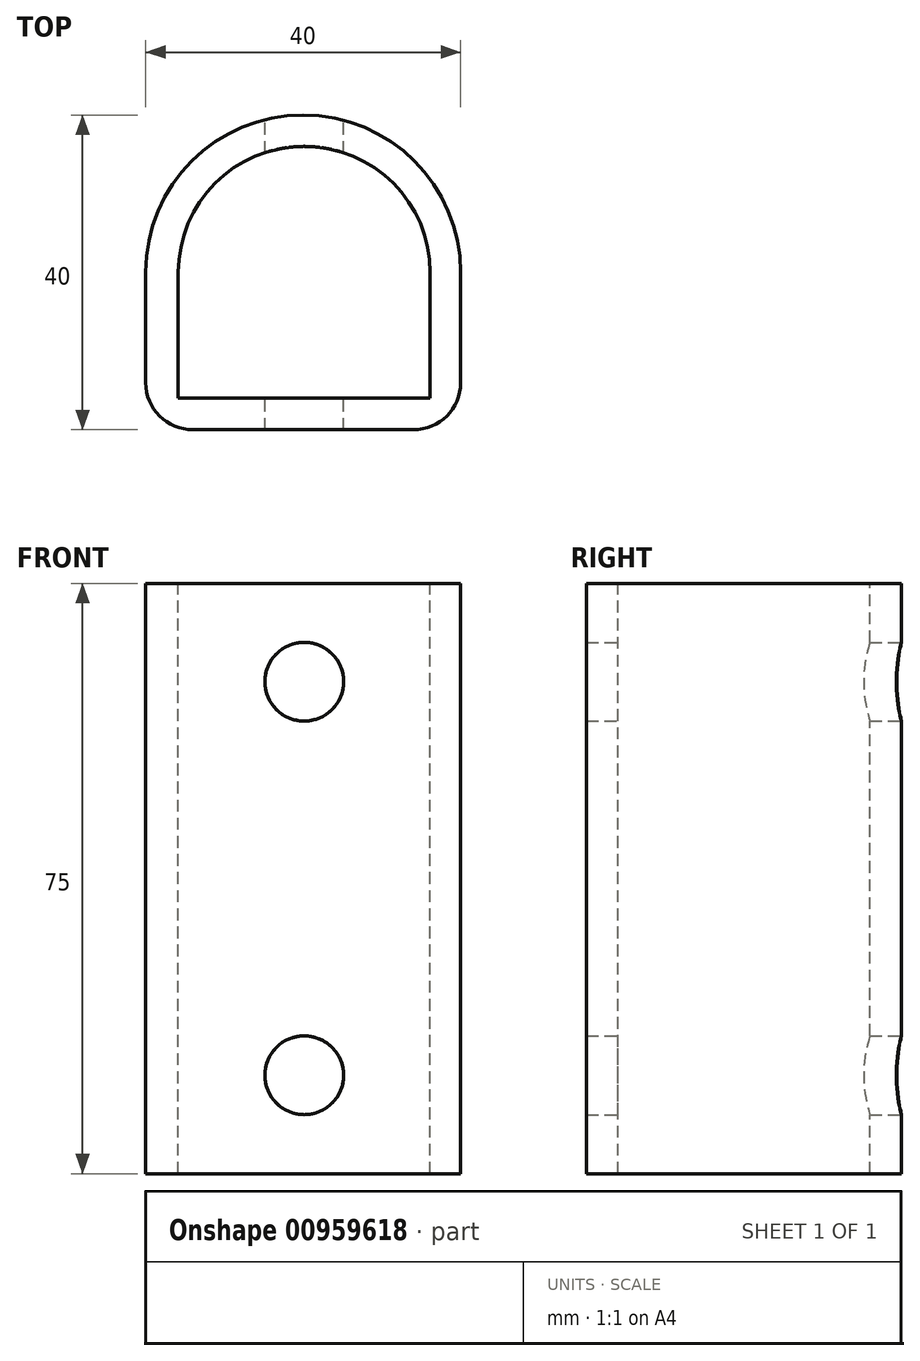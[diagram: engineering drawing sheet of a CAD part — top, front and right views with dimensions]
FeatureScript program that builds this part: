
annotation { "Feature Type Name" : "Feature", "Feature Type Description" : "" }
export const myFeature = defineFeature(function(context is Context, id is Id, definition is map)
    precondition{}
    {
        {
            var Q0;
            Q0=qCreatedBy(makeId("Top.planeOp"),FACE);
            var sketch = newSketch(context, id + "F0", { "sketchPlane" : qUnion([Q0])});
            skLineSegment(sketch, "E0", {"start": v(0, 0) * mm, "end": v(40, 0) * mm});
            skLineSegment(sketch, "E1", {"start": v(40, 0) * mm, "end": v(40, 20) * mm});
            skLineSegment(sketch, "E2", {"start": v(40, 20) * mm, "end": v(0, 20) * mm});
            skLineSegment(sketch, "E3", {"start": v(0, 20) * mm, "end": v(0, 0) * mm});
            skCircle(sketch, "E4", {"center": v(20, 20) * mm, "radius": 20 * mm});
            skSolve(sketch);
        }
        {
            var Q0;
            {var subQ0=sQuery(id+"F0.wireOp",EDGE,"E2");Q0=makeQuery(id+"F0.imprint","IMPRINT",FACE,{"disambiguationData":[TD([[makeQuery(id+"F0.imprint","IMPRINT",EDGE,{"derivedFrom":subQ0}),-1.0]])]});}
            var Q1;
            {var subQ0=sQuery(id+"F0.wireOp",EDGE,"E2");Q1=makeQuery(id+"F0.imprint","IMPRINT",FACE,{"disambiguationData":[TD([[makeQuery(id+"F0.imprint","IMPRINT",EDGE,{"derivedFrom":subQ0}),1.0]])]});}
            var Q2;
            {var subQ0=sQuery(id+"F0.wireOp",EDGE,"E1");Q2=makeQuery(id+"F0.imprint","IMPRINT",FACE,{"disambiguationData":[TD([[makeQuery(id+"F0.imprint","IMPRINT",EDGE,{"derivedFrom":subQ0}),1.0]])]});}
            var Q3;
            {var subQ0=sQuery(id+"F0.wireOp",EDGE,"E3");Q3=makeQuery(id+"F0.imprint","IMPRINT",FACE,{"disambiguationData":[TD([[makeQuery(id+"F0.imprint","IMPRINT",EDGE,{"derivedFrom":subQ0}),1.0]])]});}
            extrude(context, id + "F1", {"entities" : qUnion([Q0, Q1, Q2, Q3]), "depth" : 75 * mm, "offsetDistance" : 25 * mm});
        }
        {
            var Q0;
            Q0=makeQuery(id+"F1.opExtrude","CAP_FACE",FACE,{"disambiguationData":[OSD([sQuery(id+"F0.wireOp",EDGE,"E0"),sQuery(id+"F0.wireOp",EDGE,"E1"),sQuery(id+"F0.wireOp",EDGE,"E3"),sQuery(id+"F0.wireOp",EDGE,"E4")])],"isStart":false});
            var sketch = newSketch(context, id + "F2", { "sketchPlane" : qUnion([Q0])});
            skLineSegment(sketch, "E5.bottom", {"start": v(4.14, 20) * mm, "end": v(36.14, 20) * mm});
            skLineSegment(sketch, "E5.top", {"start": v(4.14, 4) * mm, "end": v(36.14, 4) * mm});
            skLineSegment(sketch, "E5.left", {"start": v(4.14, 20) * mm, "end": v(4.14, 4) * mm});
            skLineSegment(sketch, "E5.right", {"start": v(36.14, 20) * mm, "end": v(36.14, 4) * mm});
            skCircle(sketch, "E6", {"center": v(20.14, 20) * mm, "radius": 16 * mm});
            skSolve(sketch);
        }
        {
            var Q0;
            {var subQ0=sQuery(id+"F2.wireOp",EDGE,"E5.bottom");Q0=makeQuery(id+"F2.imprint","IMPRINT",FACE,{"disambiguationData":[TD([[makeQuery(id+"F2.imprint","IMPRINT",EDGE,{"derivedFrom":subQ0}),1.0]])]});}
            var Q1;
            {var subQ0=sQuery(id+"F2.wireOp",EDGE,"E5.bottom");Q1=makeQuery(id+"F2.imprint","IMPRINT",FACE,{"disambiguationData":[TD([[makeQuery(id+"F2.imprint","IMPRINT",EDGE,{"derivedFrom":subQ0}),-1.0]])]});}
            var Q2;
            {var subQ0=sQuery(id+"F2.wireOp",EDGE,"E5.left");Q2=makeQuery(id+"F2.imprint","IMPRINT",FACE,{"disambiguationData":[TD([[makeQuery(id+"F2.imprint","IMPRINT",EDGE,{"derivedFrom":subQ0}),1.0]])]});}
            var Q3;
            {var subQ0=sQuery(id+"F2.wireOp",EDGE,"E5.right");Q3=makeQuery(id+"F2.imprint","IMPRINT",FACE,{"disambiguationData":[TD([[makeQuery(id+"F2.imprint","IMPRINT",EDGE,{"derivedFrom":subQ0}),-1.0]])]});}
            extrude(context, id + "F3", {"entities" : qUnion([Q0, Q1, Q2, Q3]), "operationType" : NewBodyOperationType.REMOVE, "oppositeDirection" : true, "depth" : 75 * mm, "offsetDistance" : 25 * mm});
        }
        {
            var Q0;
            Q0=makeQuery(id+"F3.boolean.opBoolean","COPY",FACE,{"derivedFrom":makeQuery(id+"F3.opExtrude","SWEPT_FACE",FACE,{"disambiguationData":[OSD([sQuery(id+"F2.wireOp",EDGE,"E5.top")])]})});
            var sketch = newSketch(context, id + "F4", { "sketchPlane" : qUnion([Q0])});
            skPoint(sketch, "E7.startSnap0", {"position": v(-20.14, 0) * mm});
            skCircle(sketch, "E8", {"center": v(-20.14, 12.5) * mm, "radius": 5 * mm});
            skCircle(sketch, "E9", {"center": v(-20.14, 62.5) * mm, "radius": 5 * mm});
            skSolve(sketch);
        }
        {
            var Q0;
            Q0=makeQuery(id+"F1.opExtrude","SWEPT_EDGE",EDGE,{"disambiguationData":[OSD([sQuery(id+"F0.wireOp",EDGE,"E0"),sQuery(id+"F0.wireOp",EDGE,"E1")])]});
            fillet(context, id + "F5", {"entities" : qUnion([Q0]), "radius" : 6 * mm, "tangentPropagation" : true, "allowEdgeOverflow" : false});
        }
        {
            var Q0;
            Q0=makeQuery(id+"F1.opExtrude","SWEPT_EDGE",EDGE,{"disambiguationData":[OSD([sQuery(id+"F0.wireOp",EDGE,"E0"),sQuery(id+"F0.wireOp",EDGE,"E3")])]});
            fillet(context, id + "F6", {"entities" : qUnion([Q0]), "radius" : 6 * mm, "tangentPropagation" : true, "allowEdgeOverflow" : false});
        }
        {
            var Q0;
            Q0=makeQuery(id+"F4.imprint","IMPRINT",FACE,{"disambiguationData":[TD([[makeQuery(id+"F4.imprint","IMPRINT",EDGE,{"derivedFrom":sQuery(id+"F4.wireOp",EDGE,"E8")}),1.0]])]});
            var Q1;
            Q1=makeQuery(id+"F4.imprint","IMPRINT",FACE,{"disambiguationData":[TD([[makeQuery(id+"F4.imprint","IMPRINT",EDGE,{"derivedFrom":sQuery(id+"F4.wireOp",EDGE,"E9")}),1.0]])]});
            extrude(context, id + "F7", {"entities" : qUnion([Q0, Q1]), "operationType" : NewBodyOperationType.REMOVE, "oppositeDirection" : true, "depth" : 25 * mm, "offsetDistance" : 25 * mm, "hasSecondDirection" : true, "secondDirectionBound" : SecondDirectionBoundingType.THROUGH_ALL, "secondDirectionOppositeDirection" : false, "secondDirectionDepth" : 25 * mm});
        }
    });
